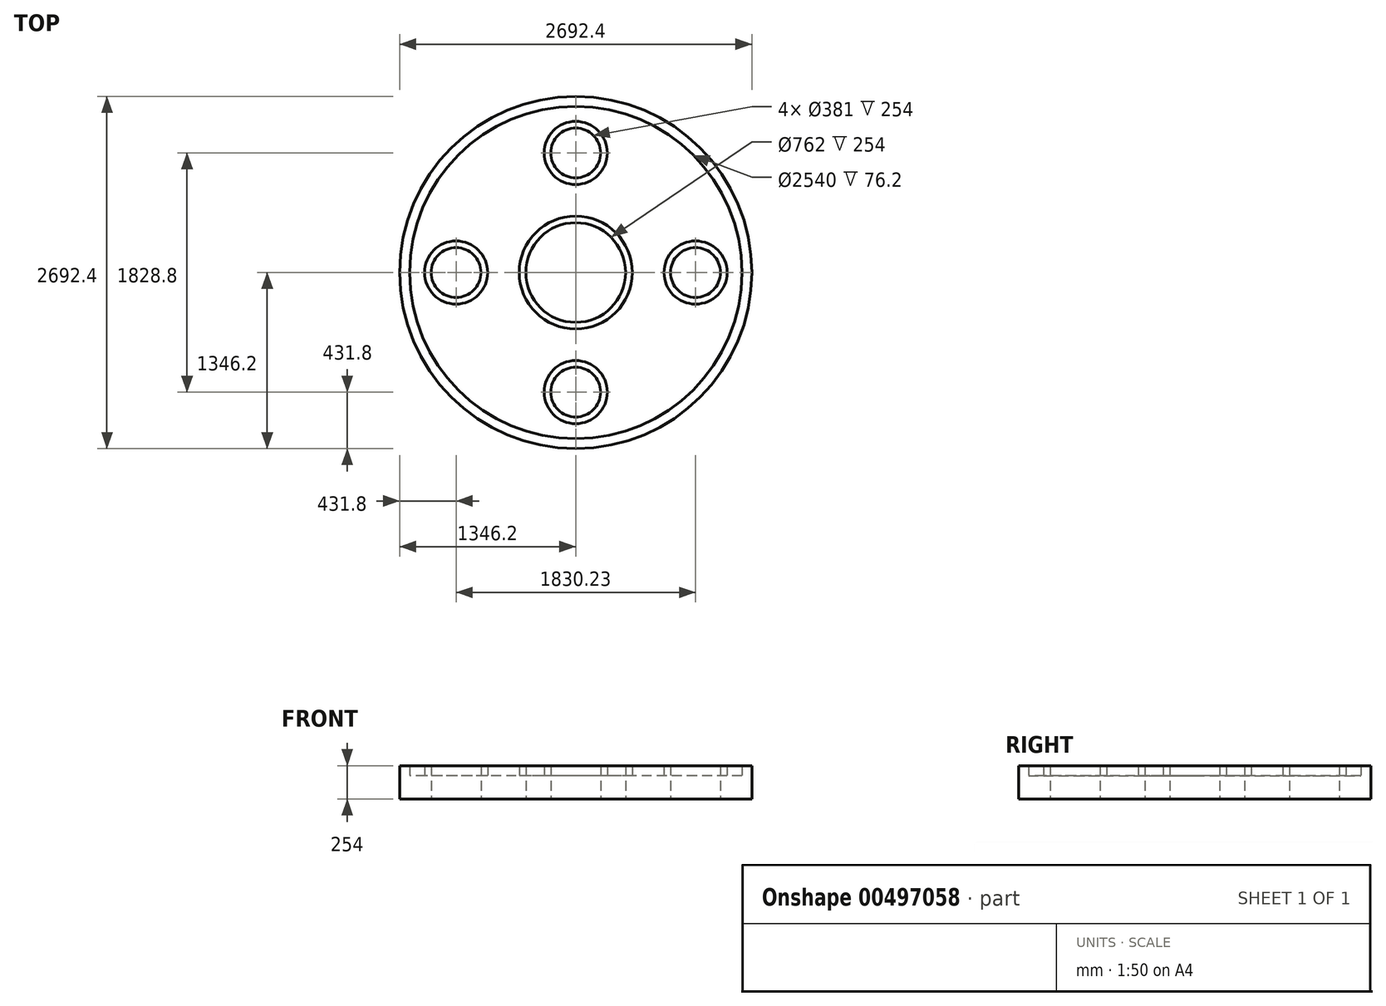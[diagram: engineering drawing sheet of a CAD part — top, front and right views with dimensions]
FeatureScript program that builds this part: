
annotation { "Feature Type Name" : "Feature", "Feature Type Description" : "" }
export const myFeature = defineFeature(function(context is Context, id is Id, definition is map)
    precondition{}
    {
        {
            var Q0;
            Q0=qCreatedBy(makeId("Top.planeOp"),FACE);
            var sketch = newSketch(context, id + "F0", { "sketchPlane" : qUnion([Q0])});
            skCircle(sketch, "E0", {"center": v(0, 0) * mm, "radius": 1270 * mm});
            skCircle(sketch, "E1.0", {"center": v(0, 0) * mm, "radius": 1346.2 * mm});
            skCircle(sketch, "E2", {"center": v(0, 0) * mm, "radius": 431.8 * mm});
            skCircle(sketch, "E3.0", {"center": v(0, 0) * mm, "radius": 381 * mm});
            skCircle(sketch, "E4", {"center": v(-914.4, 0) * mm, "radius": 190.5 * mm});
            skCircle(sketch, "E5", {"center": v(-914.4, 0) * mm, "radius": 241.3 * mm});
            skCircle(sketch, "E6", {"center": v(915.83, 0) * mm, "radius": 190.5 * mm});
            skCircle(sketch, "E7", {"center": v(915.83, 0) * mm, "radius": 241.3 * mm});
            skCircle(sketch, "E8", {"center": v(0, 914.4) * mm, "radius": 190.5 * mm});
            skCircle(sketch, "E9", {"center": v(0, 914.4) * mm, "radius": 241.3 * mm});
            skCircle(sketch, "E10", {"center": v(0, -914.4) * mm, "radius": 190.5 * mm});
            skCircle(sketch, "E11", {"center": v(0, -914.4) * mm, "radius": 241.3 * mm});
            skSolve(sketch);
        }
        {
            var Q0;
            Q0=makeQuery(id+"F0.imprint","IMPRINT",FACE,{"disambiguationData":[TD([[makeQuery(id+"F0.imprint","IMPRINT",EDGE,{"derivedFrom":sQuery(id+"F0.wireOp",EDGE,"E0")}),1.0]])]});
            extrude(context, id + "F1", {"entities" : qUnion([Q0]), "depth" : 177.8 * mm});
        }
        {
            var Q0;
            Q0=makeQuery(id+"F0.imprint","IMPRINT",FACE,{"disambiguationData":[TD([[makeQuery(id+"F0.imprint","IMPRINT",EDGE,{"derivedFrom":sQuery(id+"F0.wireOp",EDGE,"E8")}),-1.0]])]});
            var Q1;
            Q1=makeQuery(id+"F0.imprint","IMPRINT",FACE,{"disambiguationData":[TD([[makeQuery(id+"F0.imprint","IMPRINT",EDGE,{"derivedFrom":sQuery(id+"F0.wireOp",EDGE,"E6")}),-1.0]])]});
            var Q2;
            Q2=makeQuery(id+"F0.imprint","IMPRINT",FACE,{"disambiguationData":[TD([[makeQuery(id+"F0.imprint","IMPRINT",EDGE,{"derivedFrom":sQuery(id+"F0.wireOp",EDGE,"E10")}),-1.0]])]});
            var Q3;
            Q3=makeQuery(id+"F0.imprint","IMPRINT",FACE,{"disambiguationData":[TD([[makeQuery(id+"F0.imprint","IMPRINT",EDGE,{"derivedFrom":sQuery(id+"F0.wireOp",EDGE,"E4")}),-1.0]])]});
            extrude(context, id + "F2", {"entities" : qUnion([Q0, Q1, Q2, Q3]), "operationType" : NewBodyOperationType.ADD, "depth" : 254 * mm});
        }
        {
            var Q0;
            Q0=makeQuery(id+"F0.imprint","IMPRINT",FACE,{"disambiguationData":[TD([[makeQuery(id+"F0.imprint","IMPRINT",EDGE,{"derivedFrom":sQuery(id+"F0.wireOp",EDGE,"E2")}),1.0]])]});
            extrude(context, id + "F3", {"entities" : qUnion([Q0]), "operationType" : NewBodyOperationType.ADD, "depth" : 254 * mm});
        }
        {
            var Q0;
            Q0=makeQuery(id+"F0.imprint","IMPRINT",FACE,{"disambiguationData":[TD([[makeQuery(id+"F0.imprint","IMPRINT",EDGE,{"derivedFrom":sQuery(id+"F0.wireOp",EDGE,"E0")}),-1.0]])]});
            extrude(context, id + "F4", {"entities" : qUnion([Q0]), "operationType" : NewBodyOperationType.ADD, "depth" : 254 * mm});
        }
    });
